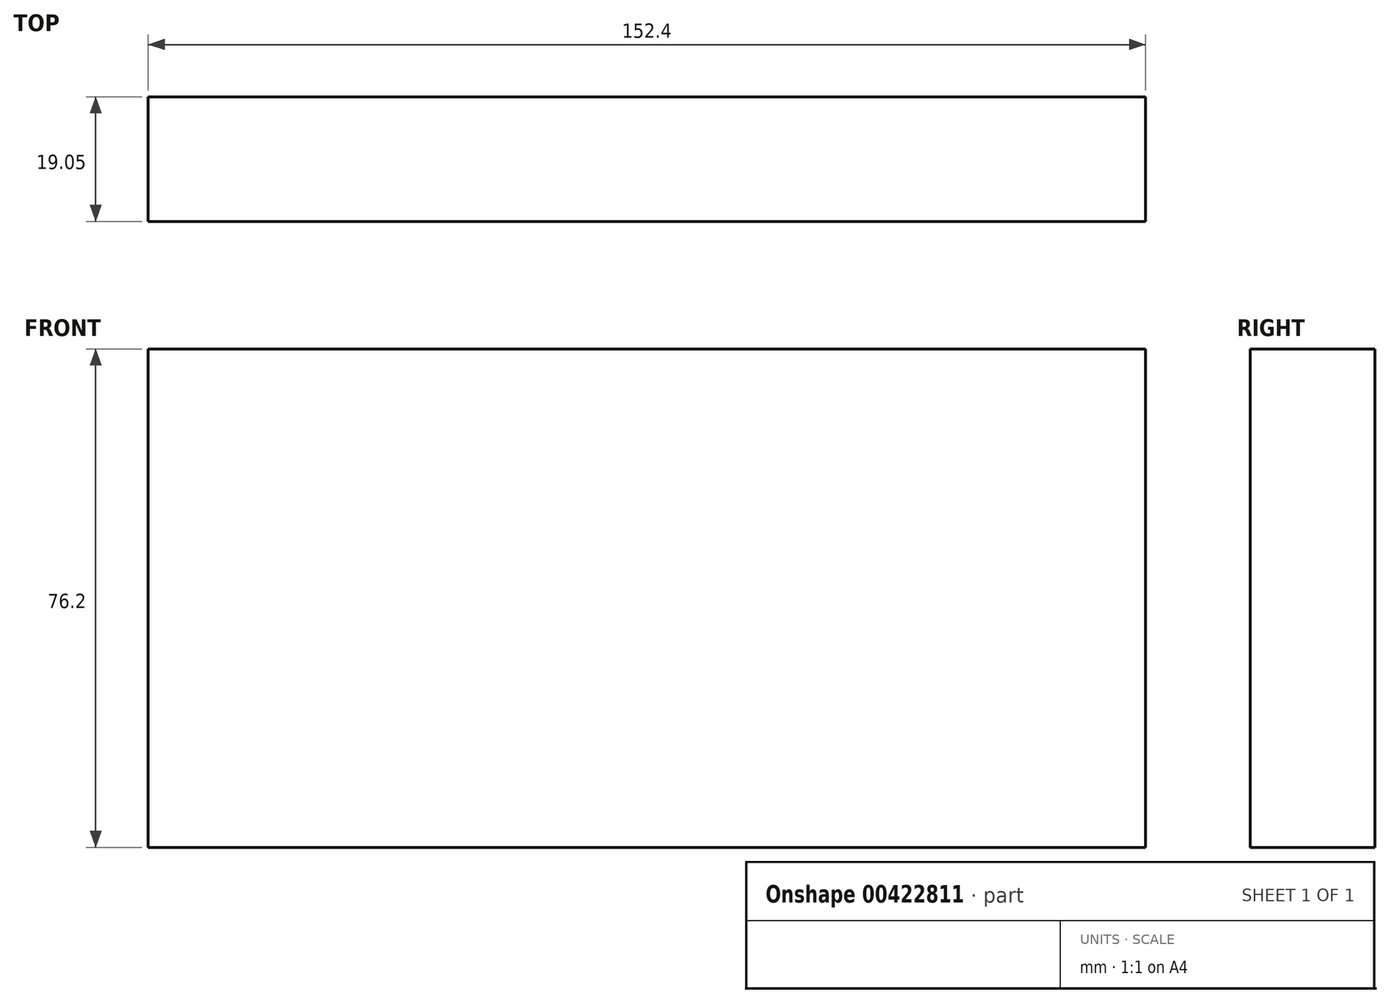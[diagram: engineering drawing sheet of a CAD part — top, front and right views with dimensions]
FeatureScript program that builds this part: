
annotation { "Feature Type Name" : "Feature", "Feature Type Description" : "" }
export const myFeature = defineFeature(function(context is Context, id is Id, definition is map)
    precondition{}
    {
        {
            var Q0;
            Q0=qCreatedBy(makeId("Front.planeOp"),FACE);
            var sketch = newSketch(context, id + "F0", { "sketchPlane" : qUnion([Q0])});
            skLineSegment(sketch, "E0.bottom", {"start": v(0, 0) * mm, "end": v(152.4, 0) * mm});
            skLineSegment(sketch, "E0.top", {"start": v(0, 76.2) * mm, "end": v(152.4, 76.2) * mm});
            skLineSegment(sketch, "E0.left", {"start": v(0, 0) * mm, "end": v(0, 76.2) * mm});
            skLineSegment(sketch, "E0.right", {"start": v(152.4, 0) * mm, "end": v(152.4, 76.2) * mm});
            skSolve(sketch);
        }
        {
            var Q0;
            Q0 = qSketchRegion(id + "F0", true);
            extrude(context, id + "F1", {"entities" : qUnion([Q0]), "depth" : 19.05 * mm});
        }
    });
